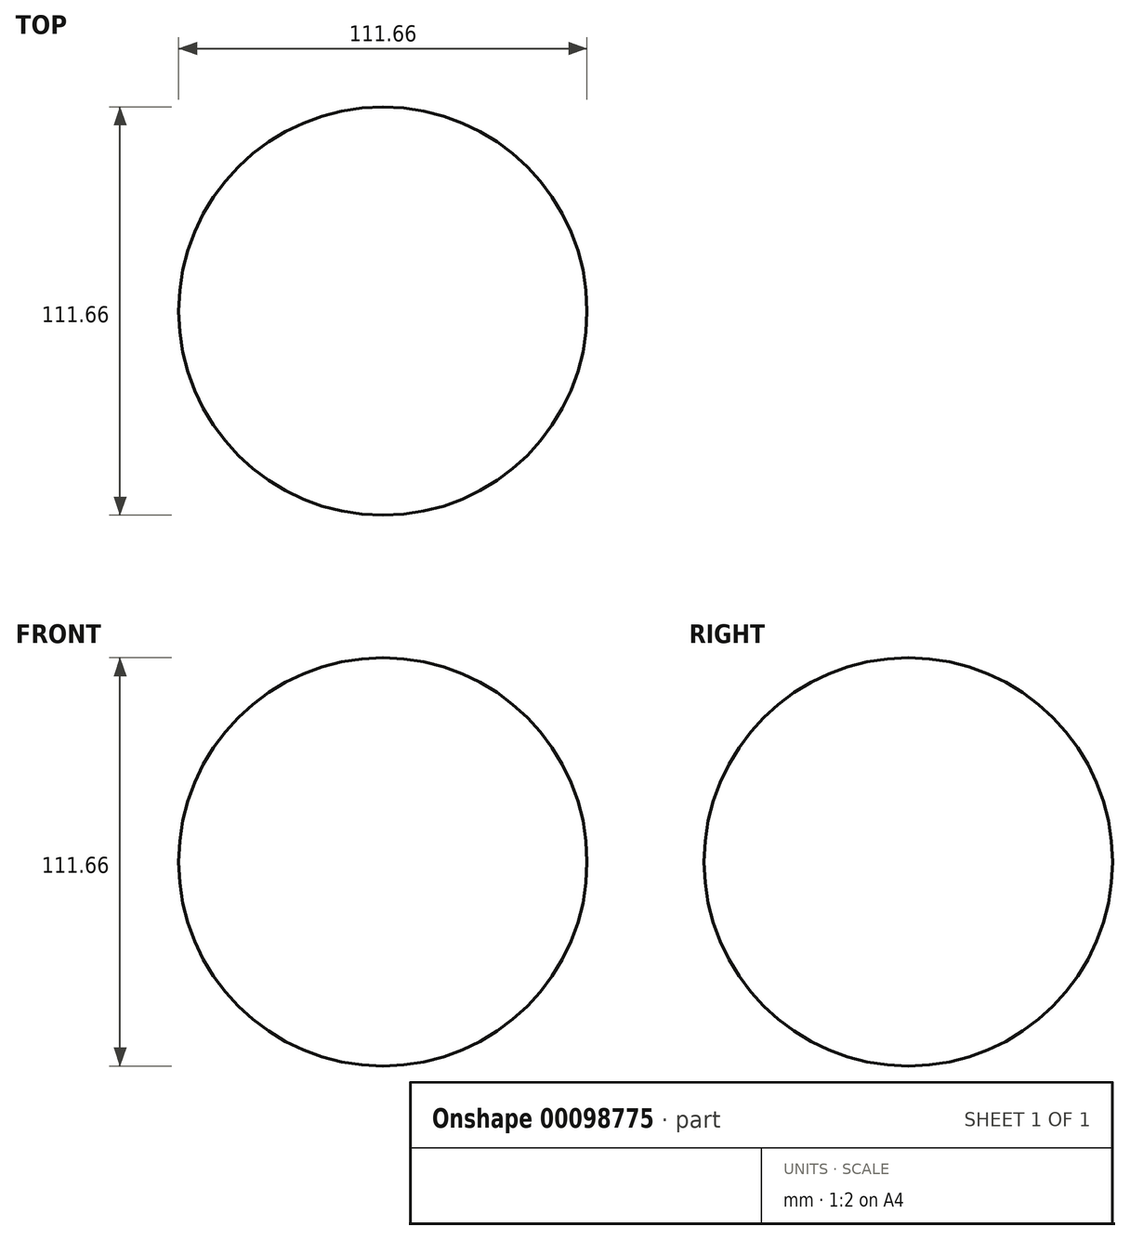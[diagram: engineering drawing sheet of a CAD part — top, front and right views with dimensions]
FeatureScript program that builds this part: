
annotation { "Feature Type Name" : "Feature", "Feature Type Description" : "" }
export const myFeature = defineFeature(function(context is Context, id is Id, definition is map)
    precondition{}
    {
        {
            var Q0;
            Q0=qCreatedBy(makeId("Front.planeOp"),FACE);
            var sketch = newSketch(context, id + "F0", { "sketchPlane" : qUnion([Q0])});
            skCircle(sketch, "E0", {"center": v(0, 0) * mm, "radius": 55.83 * mm});
            skLineSegment(sketch, "E1", {"start": v(0, 55.83) * mm, "end": v(0, -55.83) * mm});
            skSolve(sketch);
        }
        {
            var Q0;
            {var subQ0=sQuery(id+"F0.wireOp",EDGE,"E1");Q0=makeQuery(id+"F0.imprint","IMPRINT",FACE,{"disambiguationData":[TD([[makeQuery(id+"F0.imprint","IMPRINT",EDGE,{"derivedFrom":subQ0}),1.0]])]});}
            var Q1;
            Q1=sQuery(id+"F0.wireOp",EDGE,"E1");
            revolve(context, id + "F1", {"entities" : qUnion([Q0]), "axis" : qUnion([Q1]), "revolveType" : RevolveType.FULL});
        }
    });
